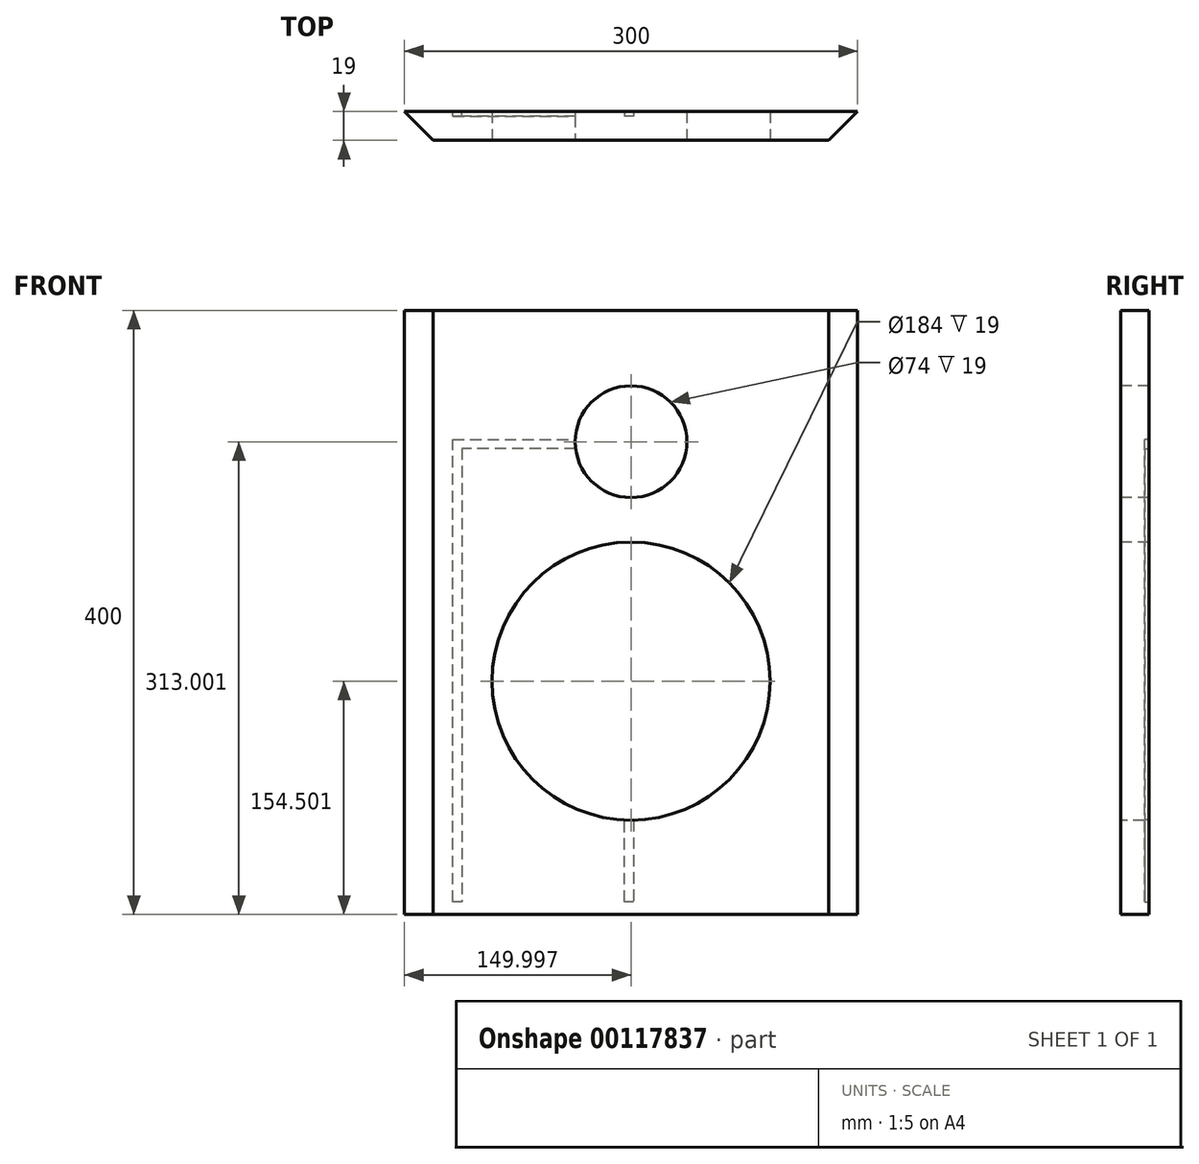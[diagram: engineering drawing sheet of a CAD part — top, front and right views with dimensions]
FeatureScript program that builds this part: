
annotation { "Feature Type Name" : "Feature", "Feature Type Description" : "" }
export const myFeature = defineFeature(function(context is Context, id is Id, definition is map)
    precondition{}
    {
        {
            var Q0;
            Q0=qCreatedBy(makeId("Front.planeOp"),FACE);
            var sketch = newSketch(context, id + "F0", { "sketchPlane" : qUnion([Q0])});
            skLineSegment(sketch, "E0.bottom", {"start": v(-250.04, 196.75) * mm, "end": v(49.96, 196.75) * mm});
            skLineSegment(sketch, "E0.top", {"start": v(-250.04, -203.25) * mm, "end": v(49.96, -203.25) * mm});
            skLineSegment(sketch, "E0.left", {"start": v(-250.04, 196.75) * mm, "end": v(-250.04, -203.25) * mm});
            skLineSegment(sketch, "E0.right", {"start": v(49.96, 196.75) * mm, "end": v(49.96, -203.25) * mm});
            skSolve(sketch);
        }
        {
            var Q0;
            Q0=makeQuery(id+"F0.imprint","IMPRINT",FACE,{"disambiguationData":[TD([[makeQuery(id+"F0.imprint","IMPRINT",EDGE,{"derivedFrom":sQuery(id+"F0.wireOp",EDGE,"E0.bottom")}),-1.0]])]});
            extrude(context, id + "F1", {"entities" : qUnion([Q0]), "depth" : 19 * mm});
        }
        {
            var Q0;
            Q0=makeQuery(id+"F1.opExtrude","CAP_FACE",FACE,{"disambiguationData":[OSD([sQuery(id+"F0.wireOp",EDGE,"E0.bottom"),sQuery(id+"F0.wireOp",EDGE,"E0.top"),sQuery(id+"F0.wireOp",EDGE,"E0.left"),sQuery(id+"F0.wireOp",EDGE,"E0.right")])],"isStart":false});
            var sketch = newSketch(context, id + "F2", { "sketchPlane" : qUnion([Q0])});
            skCircle(sketch, "E1", {"center": v(-100.04, 109.75) * mm, "radius": 37 * mm});
            skPoint(sketch, "E1.centerSnap0", {"position": v(-100.04, 196.75) * mm});
            skCircle(sketch, "E2", {"center": v(-100.04, -48.75) * mm, "radius": 92 * mm});
            skPoint(sketch, "E2.centerSnap0", {"position": v(-100.04, -203.25) * mm});
            skSolve(sketch);
        }
        {
            var Q0;
            Q0=makeQuery(id+"F2.imprint","IMPRINT",FACE,{"disambiguationData":[TD([[makeQuery(id+"F2.imprint","IMPRINT",EDGE,{"derivedFrom":sQuery(id+"F2.wireOp",EDGE,"E1")}),1.0]])]});
            var Q1;
            Q1=makeQuery(id+"F2.imprint","IMPRINT",FACE,{"disambiguationData":[TD([[makeQuery(id+"F2.imprint","IMPRINT",EDGE,{"derivedFrom":sQuery(id+"F2.wireOp",EDGE,"E2")}),1.0]])]});
            extrude(context, id + "F3", {"entities" : qUnion([Q0, Q1]), "operationType" : NewBodyOperationType.REMOVE, "oppositeDirection" : true, "depth" : 19 * mm});
        }
        {
            var Q0;
            Q0=makeQuery(id+"F1.opExtrude","CAP_EDGE",EDGE,{"disambiguationData":[OSD([sQuery(id+"F0.wireOp",EDGE,"E0.left")])],"isStart":false});
            var Q1;
            Q1=makeQuery(id+"F1.opExtrude","CAP_EDGE",EDGE,{"disambiguationData":[OSD([sQuery(id+"F0.wireOp",EDGE,"E0.right")])],"isStart":false});
            chamfer(context, id + "F4", {"entities" : qUnion([Q0, Q1]), "width" : 19 * mm, "tangentPropagation" : true});
        }
        {
            var Q0;
            Q0=makeQuery(id+"F1.opExtrude","CAP_FACE",FACE,{"disambiguationData":[OSD([sQuery(id+"F0.wireOp",EDGE,"E0.bottom"),sQuery(id+"F0.wireOp",EDGE,"E0.top"),sQuery(id+"F0.wireOp",EDGE,"E0.left"),sQuery(id+"F0.wireOp",EDGE,"E0.right")])],"isStart":true});
            var sketch = newSketch(context, id + "F5", { "sketchPlane" : qUnion([Q0])});
            skLineSegment(sketch, "E3", {"start": v(136.77, 105.25) * mm, "end": v(212.04, 105.25) * mm});
            skLineSegment(sketch, "E4", {"start": v(212.04, 105.25) * mm, "end": v(212.04, -194.75) * mm});
            skLineSegment(sketch, "E5", {"start": v(212.04, -194.75) * mm, "end": v(218.04, -194.75) * mm});
            skLineSegment(sketch, "E6", {"start": v(218.04, -194.75) * mm, "end": v(218.04, 111.25) * mm});
            skLineSegment(sketch, "E7", {"start": v(218.04, 111.25) * mm, "end": v(136.77, 111.25) * mm});
            skLineSegment(sketch, "E8", {"start": v(136.77, 111.25) * mm, "end": v(136.77, 105.25) * mm});
            skSolve(sketch);
        }
        {
            var Q0;
            Q0 = qSketchRegion(id + "F5", true);
            extrude(context, id + "F6", {"entities" : qUnion([Q0]), "operationType" : NewBodyOperationType.REMOVE, "oppositeDirection" : true, "depth" : 3 * mm});
        }
        {
            var Q0;
            Q0=makeQuery(id+"F1.opExtrude","CAP_FACE",FACE,{"disambiguationData":[OSD([sQuery(id+"F0.wireOp",EDGE,"E0.bottom"),sQuery(id+"F0.wireOp",EDGE,"E0.top"),sQuery(id+"F0.wireOp",EDGE,"E0.left"),sQuery(id+"F0.wireOp",EDGE,"E0.right")])],"isStart":true});
            var sketch = newSketch(context, id + "F7", { "sketchPlane" : qUnion([Q0])});
            skLineSegment(sketch, "E9", {"start": v(98.54, -130.08) * mm, "end": v(98.54, -194.75) * mm});
            skLineSegment(sketch, "E10", {"start": v(98.54, -194.75) * mm, "end": v(104.54, -194.75) * mm});
            skLineSegment(sketch, "E11", {"start": v(104.54, -194.75) * mm, "end": v(104.54, -130.08) * mm});
            skLineSegment(sketch, "E12", {"start": v(104.54, -130.08) * mm, "end": v(98.54, -130.08) * mm});
            skSolve(sketch);
        }
        {
            var Q0;
            Q0 = qSketchRegion(id + "F7", true);
            extrude(context, id + "F8", {"entities" : qUnion([Q0]), "operationType" : NewBodyOperationType.REMOVE, "oppositeDirection" : true, "depth" : 3 * mm});
        }
    });
